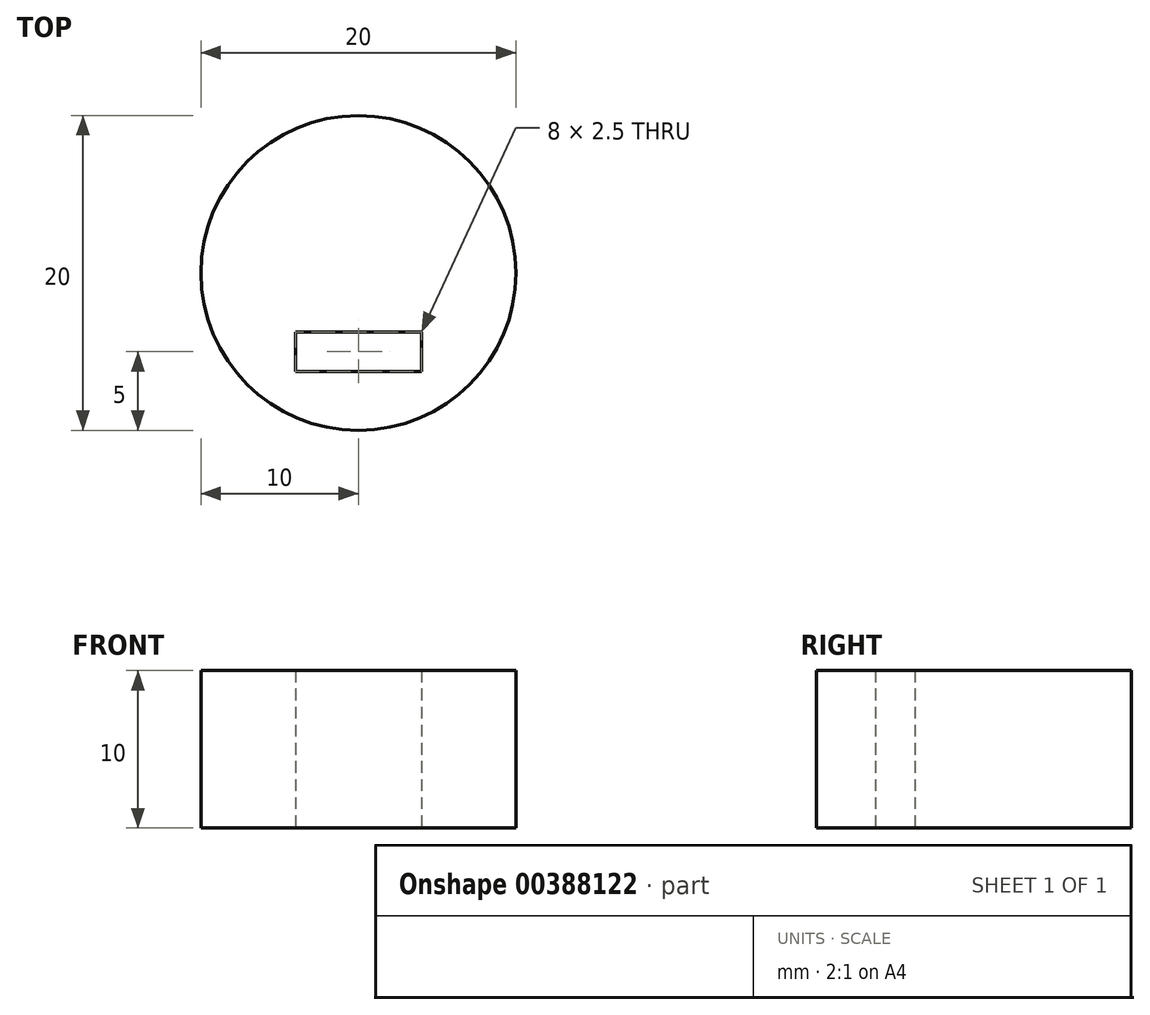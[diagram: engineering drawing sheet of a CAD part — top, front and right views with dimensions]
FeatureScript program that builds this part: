
annotation { "Feature Type Name" : "Feature", "Feature Type Description" : "" }
export const myFeature = defineFeature(function(context is Context, id is Id, definition is map)
    precondition{}
    {
        {
            var Q0;
            Q0=qCreatedBy(makeId("Top.planeOp"),FACE);
            var sketch = newSketch(context, id + "F0", { "sketchPlane" : qUnion([Q0])});
            skCircle(sketch, "E0", {"center": v(0, 0) * mm, "radius": 10 * mm});
            skLineSegment(sketch, "E1.bottom", {"start": v(4, -3.75) * mm, "end": v(-4, -3.75) * mm});
            skLineSegment(sketch, "E1.top", {"start": v(4, -6.25) * mm, "end": v(-4, -6.25) * mm});
            skLineSegment(sketch, "E1.left", {"start": v(4, -3.75) * mm, "end": v(4, -6.25) * mm});
            skLineSegment(sketch, "E1.right", {"start": v(-4, -3.75) * mm, "end": v(-4, -6.25) * mm});
            skPoint(sketch, "E1.middle", {"position": v(0, -5) * mm});
            skSolve(sketch);
        }
        {
            var Q0;
            Q0 = qSketchRegion(id + "F0", true);
            extrude(context, id + "F1", {"entities" : qUnion([Q0]), "depth" : 10 * mm});
        }
    });
